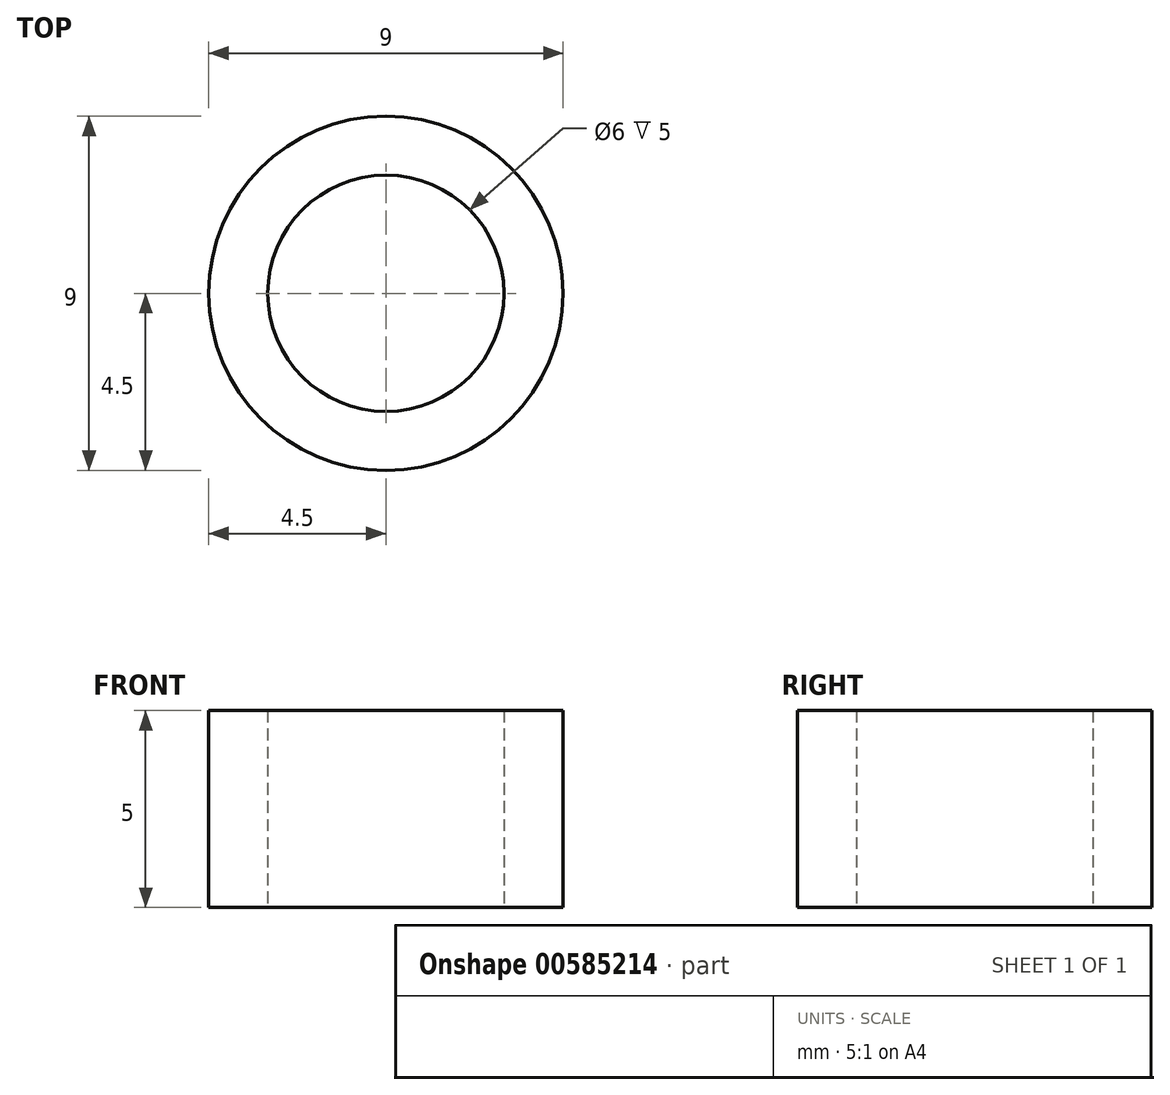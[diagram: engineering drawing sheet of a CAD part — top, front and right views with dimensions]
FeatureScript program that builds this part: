
annotation { "Feature Type Name" : "Feature", "Feature Type Description" : "" }
export const myFeature = defineFeature(function(context is Context, id is Id, definition is map)
    precondition{}
    {
        {
            var Q0;
            Q0=qCreatedBy(makeId("Top.planeOp"),FACE);
            var sketch = newSketch(context, id + "F0", { "sketchPlane" : qUnion([Q0])});
            skCircle(sketch, "E0", {"center": v(0, 5.17) * mm, "radius": 4.5 * mm});
            skCircle(sketch, "E1", {"center": v(0, 5.17) * mm, "radius": 3 * mm});
            skSolve(sketch);
        }
        {
            var Q0;
            Q0 = qSketchRegion(id + "F0", true);
            extrude(context, id + "F1", {"entities" : qUnion([Q0]), "depth" : 5 * mm, "offsetDistance" : 25 * mm});
        }
    });
